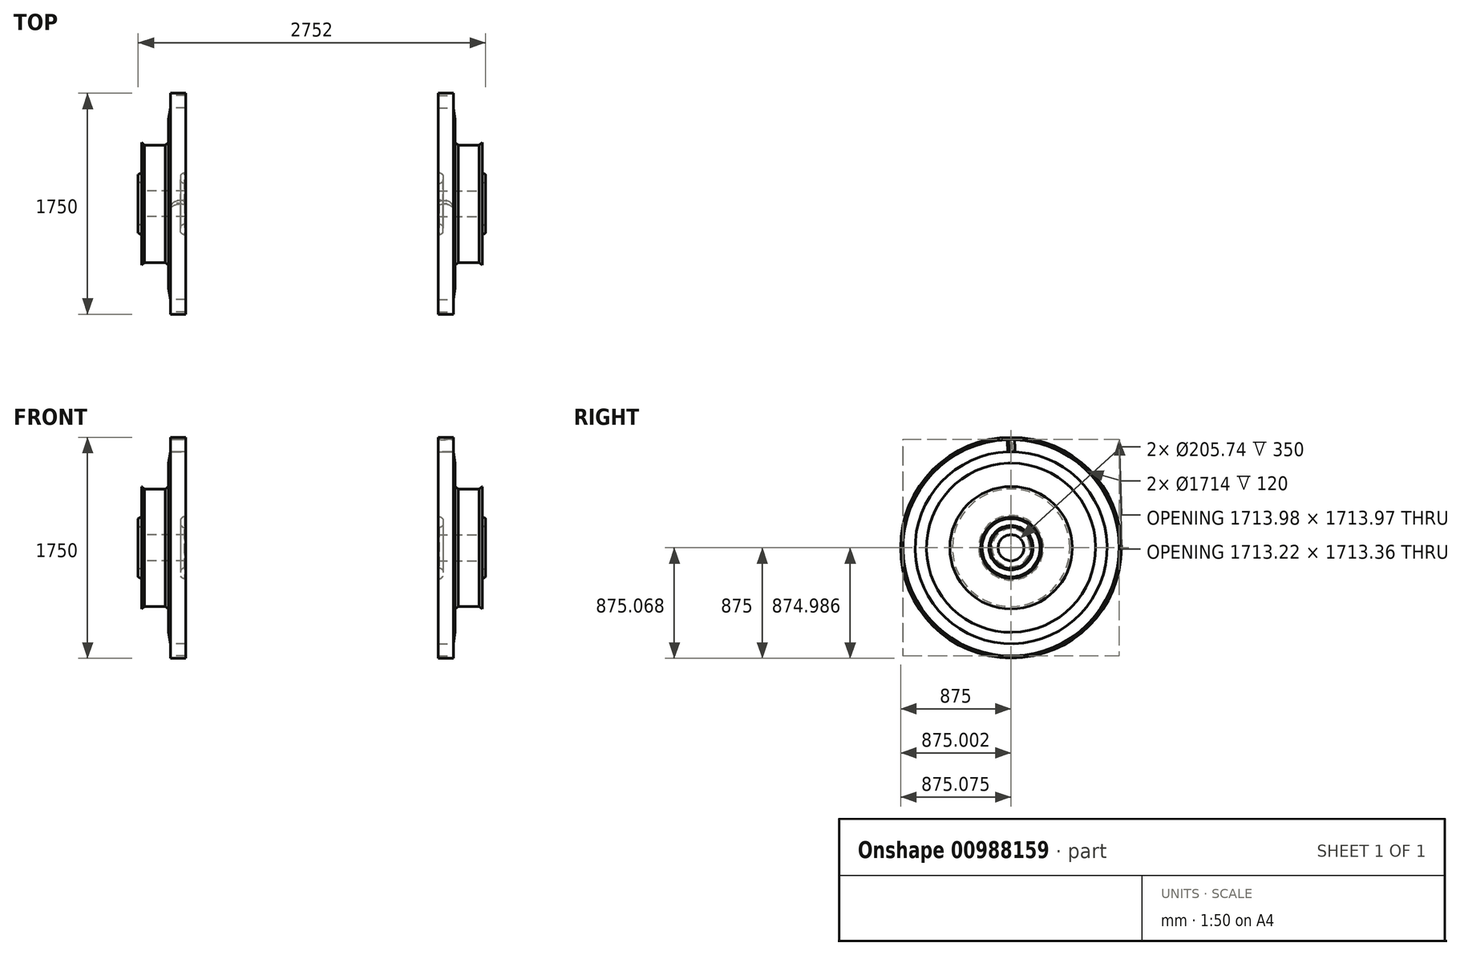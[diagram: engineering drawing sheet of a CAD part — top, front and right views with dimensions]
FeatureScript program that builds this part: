
annotation { "Feature Type Name" : "Feature", "Feature Type Description" : "" }
export const myFeature = defineFeature(function(context is Context, id is Id, definition is map)
    precondition{}
    {
        {
            var Q0;
            Q0=qCreatedBy(makeId("Top.planeOp"),FACE);
            var sketch = newSketch(context, id + "F0", { "sketchPlane" : qUnion([Q0])});
            skLineSegment(sketch, "E0", {"start": v(-458.73, 0) * mm, "end": v(0, 0) * mm, "construction": true});
            skLineSegment(sketch, "E1", {"start": v(0, 760) * mm, "end": v(-120, 760) * mm});
            skLineSegment(sketch, "E2", {"start": v(-160, 465) * mm, "end": v(-325, 465) * mm});
            skLineSegment(sketch, "E3", {"start": v(-325, 465) * mm, "end": v(-350, 485) * mm});
            skLineSegment(sketch, "E4", {"start": v(-350, 485) * mm, "end": v(-350, 240.87) * mm});
            skLineSegment(sketch, "E5", {"start": v(-350, 102.87) * mm, "end": v(0, 102.87) * mm});
            skLineSegment(sketch, "E6", {"start": v(0, 102.87) * mm, "end": v(0, 157.87) * mm});
            skLineSegment(sketch, "E7", {"start": v(-120, 875) * mm, "end": v(-120, 857) * mm});
            skLineSegment(sketch, "E8", {"start": v(-120, 857) * mm, "end": v(0, 857) * mm});
            skLineSegment(sketch, "E9", {"start": v(0, 857) * mm, "end": v(0, 875) * mm});
            skLineSegment(sketch, "E10", {"start": v(0, 875) * mm, "end": v(-120, 875) * mm});
            skLineSegment(sketch, "E11", {"start": v(-120, 760) * mm, "end": v(-120, 857) * mm, "construction": true});
            skLineSegment(sketch, "E12", {"start": v(-135, 485) * mm, "end": v(-135, 670) * mm});
            skLineSegment(sketch, "E13", {"start": v(-135, 670) * mm, "end": v(-120, 760) * mm});
            skLineSegment(sketch, "E14", {"start": v(-135, 485) * mm, "end": v(-160, 465) * mm});
            skLineSegment(sketch, "E15", {"start": v(-135, 485) * mm, "end": v(-350, 485) * mm, "construction": true});
            skArc(sketch, "E16", {"start": v(-350, 164.87) * mm, "mid": v(-363.98, 167.54) * mm, "end": v(-376, 175.16) * mm});
            skLineSegment(sketch, "E17", {"start": v(-376, 230.58) * mm, "end": v(-376, 175.16) * mm});
            skArc(sketch, "E18.trimOffspring", {"start": v(-376, 230.58) * mm, "mid": v(-363.98, 238.2) * mm, "end": v(-350, 240.87) * mm});
            skLineSegment(sketch, "E19.trimOffspring", {"start": v(-350, 164.87) * mm, "end": v(-350, 102.87) * mm});
            skArc(sketch, "E20", {"start": v(-350, 164.87) * mm, "mid": v(-388, 202.87) * mm, "end": v(-350, 240.87) * mm, "construction": true});
            skLineSegment(sketch, "E21", {"start": v(-350, 202.87) * mm, "end": v(0, 202.87) * mm, "construction": true});
            skArc(sketch, "E22", {"start": v(0, 157.87) * mm, "mid": v(-22.53, 163.91) * mm, "end": v(-39, 180.42) * mm});
            skLineSegment(sketch, "E23", {"start": v(-39, 225.32) * mm, "end": v(-39, 180.42) * mm});
            skArc(sketch, "E24.trimOffspring", {"start": v(-39, 225.32) * mm, "mid": v(-22.53, 241.83) * mm, "end": v(0, 247.87) * mm});
            skLineSegment(sketch, "E25.trimOffspring", {"start": v(0, 247.87) * mm, "end": v(0, 760) * mm});
            skArc(sketch, "E26", {"start": v(0, 157.87) * mm, "mid": v(-45, 202.87) * mm, "end": v(0, 247.87) * mm, "construction": true});
            skSolve(sketch);
        }
        {
            var Q0;
            Q0=makeQuery(id+"F0.imprint","IMPRINT",FACE,{"disambiguationData":[TD([[makeQuery(id+"F0.imprint","IMPRINT",EDGE,{"derivedFrom":sQuery(id+"F0.wireOp",EDGE,"E7")}),1.0]])]});
            var Q1;
            Q1=makeQuery(id+"F0.imprint","IMPRINT",FACE,{"disambiguationData":[TD([[makeQuery(id+"F0.imprint","IMPRINT",EDGE,{"derivedFrom":sQuery(id+"F0.wireOp",EDGE,"E1")}),1.0]])]});
            var Q2;
            Q2=sQuery(id+"F0.wireOp",EDGE,"E0");
            revolve(context, id + "F1", {"surfaceOperationType" : NewSurfaceOperationType.NEW, "entities" : qUnion([Q0, Q1]), "axis" : qUnion([Q2]), "revolveType" : RevolveType.FULL});
        }
        {
            var Q0;
            Q0=makeQuery(id+"F1.opRevolve","SWEPT_EDGE",EDGE,{"disambiguationData":[OSD([sQuery(id+"F0.wireOp",EDGE,"E24.trimOffspring"),sQuery(id+"F0.wireOp",EDGE,"E25.trimOffspring")])]});
            var Q1;
            Q1=makeQuery(id+"F1.opRevolve","SWEPT_EDGE",EDGE,{"disambiguationData":[OSD([sQuery(id+"F0.wireOp",EDGE,"E6"),sQuery(id+"F0.wireOp",EDGE,"E22")])]});
            chamfer(context, id + "F2", {"entities" : qUnion([Q0, Q1]), "width" : 9 * mm, "tangentPropagation" : true});
        }
        {
            var Q0;
            Q0=qCreatedBy(makeId("Right.planeOp"),FACE);
            var sketch = newSketch(context, id + "F3", { "sketchPlane" : qUnion([Q0])});
            skLineSegment(sketch, "E27", {"start": v(0, 0) * mm, "end": v(0, 760) * mm, "construction": true});
            skLineSegment(sketch, "E28", {"start": v(0, 0) * mm, "end": v(0, 875) * mm, "construction": true});
            skCircle(sketch, "E29.0", {"center": v(0, 0) * mm, "radius": 875 * mm, "construction": true});
            skCircle(sketch, "E30.0", {"center": v(0, 0) * mm, "radius": 760 * mm, "construction": true});
            skSolve(sketch);
        }
        {
            var Q0;
            Q0=sQuery(id+"F3.wireOp",VERTEX,"E28.end");
            var Q1;
            Q1=sQuery(id+"F3.wireOp",EDGE,"E28");
            cPlane(context, id + "F4", {"entities" : qUnion([Q0, Q1]), "cplaneType" : CPlaneType.LINE_POINT, "offset" : 25 * mm, "width" : 150 * mm, "height" : 150 * mm});
        }
        {
            var Q0;
            Q0=sQuery(id+"F3.wireOp",VERTEX,"E27.end");
            var Q1;
            Q1=sQuery(id+"F3.wireOp",EDGE,"E28");
            cPlane(context, id + "F5", {"entities" : qUnion([Q0, Q1]), "cplaneType" : CPlaneType.LINE_POINT, "offset" : 25 * mm, "width" : 150 * mm, "height" : 150 * mm});
        }
        {
            var Q0;
            Q0=qCreatedBy(id+"F5.planeOp",FACE);
            cPlane(context, id + "F6", {"entities" : qUnion([Q0]), "cplaneType" : CPlaneType.OFFSET, "offset" : 1 * mm, "oppositeDirection" : true, "width" : 150 * mm, "height" : 150 * mm});
        }
        {
            var Q0;
            Q0=qCreatedBy(id+"F4.planeOp",FACE);
            cPlane(context, id + "F7", {"entities" : qUnion([Q0]), "cplaneType" : CPlaneType.OFFSET, "offset" : 5 * mm, "oppositeDirection" : true, "width" : 150 * mm, "height" : 150 * mm});
        }
        {
            var Q0;
            Q0=qCreatedBy(id+"F6.planeOp",FACE);
            var sketch = newSketch(context, id + "F8", { "sketchPlane" : qUnion([Q0])});
            skLineSegment(sketch, "E31.0", {"start": v(-120, -760) * mm, "end": v(-120, 760) * mm, "construction": true});
            skLineSegment(sketch, "E32.0", {"start": v(0, 760) * mm, "end": v(0, -760) * mm, "construction": true});
            skLineSegment(sketch, "E33", {"start": v(0, 0) * mm, "end": v(0, 15) * mm});
            skLineSegment(sketch, "E34", {"start": v(-120, -15.15) * mm, "end": v(-120, -25.15) * mm});
            skFitSpline(sketch, "E35", {"points": [v(0, 15) * mm, v(-42.55, 31.64) * mm, v(-89.52, 15) * mm, v(-120, -15.15) * mm], "startDerivative": vector(-92.64, 151.4) * mm, "endDerivative": vector(-83.79, -129.37) * mm});
            skFitSpline(sketch, "E36", {"points": [v(0, 0) * mm, v(-22.07, -5.15) * mm, v(-58.4, 2.79) * mm, v(-120, -25.15) * mm], "startDerivative": vector(-93.31, -94.72) * mm, "endDerivative": vector(-145.88, -146.48) * mm});
            skSolve(sketch);
        }
        {
            var Q0;
            Q0=qCreatedBy(id+"F7.planeOp",FACE);
            var sketch = newSketch(context, id + "F9", { "sketchPlane" : qUnion([Q0])});
            skLineSegment(sketch, "E37.0", {"start": v(0, 875) * mm, "end": v(0, -875) * mm, "construction": true});
            skLineSegment(sketch, "E38.0", {"start": v(-120, -875) * mm, "end": v(-120, 875) * mm, "construction": true});
            skLineSegment(sketch, "E39", {"start": v(-120, -21.54) * mm, "end": v(-120, -31.54) * mm});
            skLineSegment(sketch, "E40", {"start": v(0, 6) * mm, "end": v(0, -9) * mm});
            skFitSpline(sketch, "E41", {"points": [v(0, 6) * mm, v(-42.35, 27.2) * mm, v(-88.54, 10.35) * mm, v(-120, -21.54) * mm], "startDerivative": vector(-97.55, 132.95) * mm, "endDerivative": vector(-73.28, -144.94) * mm});
            skFitSpline(sketch, "E42", {"points": [v(0, -9) * mm, v(-39.82, -8.5) * mm, v(-73.33, -5.96) * mm, v(-120, -31.54) * mm], "startDerivative": vector(-80.99, -68.84) * mm, "endDerivative": vector(-104.84, -82.75) * mm});
            skSolve(sketch);
        }
        {
            var Q2;
            Q2=qSketchRegion(id+"F8",true);
            var Q3;
            Q3=qSketchRegion(id+"F9",true);
            loft(context, id + "F10", {"operationType" : NewBodyOperationType.ADD, "sheetProfilesArray" : [{ "sheetProfileEntities" : qUnion([Q2]) }, { "sheetProfileEntities" : qUnion([Q3]) }]});
        }
        {
            var Q0;
            Q0=qCreatedBy(makeId("Right.planeOp"),FACE);
            cPlane(context, id + "F11", {"entities" : qUnion([Q0]), "cplaneType" : CPlaneType.OFFSET, "offset" : 1000 * mm, "width" : 150 * mm, "height" : 150 * mm});
        }
        {
            var Q0;
            Q0=makeQuery(id+"F1.opRevolve","SWEPT_BODY",BODY,{"disambiguationData":[OSD([sQuery(id+"F0.wireOp",EDGE,"E1"),sQuery(id+"F0.wireOp",EDGE,"E2"),sQuery(id+"F0.wireOp",EDGE,"E3"),sQuery(id+"F0.wireOp",EDGE,"E4"),sQuery(id+"F0.wireOp",EDGE,"E5"),sQuery(id+"F0.wireOp",EDGE,"E6"),sQuery(id+"F0.wireOp",EDGE,"E12"),sQuery(id+"F0.wireOp",EDGE,"E13"),sQuery(id+"F0.wireOp",EDGE,"E14"),sQuery(id+"F0.wireOp",EDGE,"E16"),sQuery(id+"F0.wireOp",EDGE,"E17"),sQuery(id+"F0.wireOp",EDGE,"E18.trimOffspring"),sQuery(id+"F0.wireOp",EDGE,"E19.trimOffspring"),sQuery(id+"F0.wireOp",EDGE,"E22"),sQuery(id+"F0.wireOp",EDGE,"E23"),sQuery(id+"F0.wireOp",EDGE,"E24.trimOffspring"),sQuery(id+"F0.wireOp",EDGE,"E25.trimOffspring")])]});
            var Q1;
            Q1=qCreatedBy(id+"F11.planeOp",FACE);
            mirror(context, id + "F12", {"entities" : qUnion([Q0]), "mirrorPlane" : qUnion([Q1])});
        }
    });
